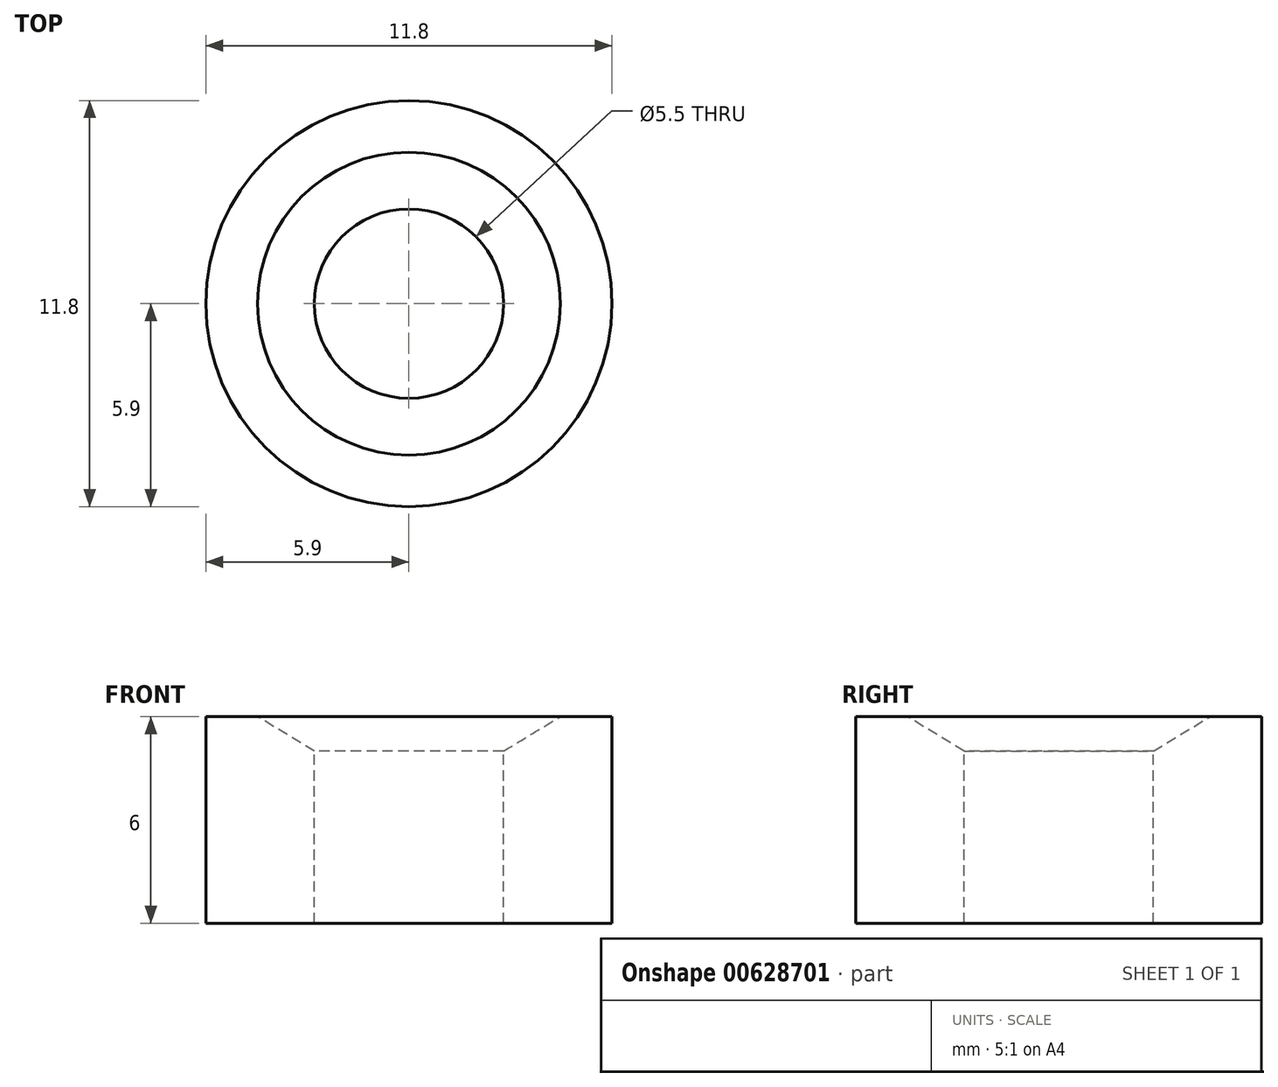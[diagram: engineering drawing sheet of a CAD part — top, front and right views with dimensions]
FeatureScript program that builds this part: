
annotation { "Feature Type Name" : "Feature", "Feature Type Description" : "" }
export const myFeature = defineFeature(function(context is Context, id is Id, definition is map)
    precondition{}
    {
        {
            var Q0;
            Q0=qCreatedBy(makeId("Front.planeOp"),FACE);
            var sketch = newSketch(context, id + "F0", { "sketchPlane" : qUnion([Q0])});
            skLineSegment(sketch, "E0", {"start": v(0, 40.85) * mm, "end": v(0, -41.9) * mm, "construction": true});
            skLineSegment(sketch, "E1", {"start": v(-5.9, 3) * mm, "end": v(-4.4, 3) * mm});
            skLineSegment(sketch, "E2", {"start": v(-4.4, 3) * mm, "end": v(-2.75, 2) * mm});
            skLineSegment(sketch, "E3", {"start": v(-2.75, 2) * mm, "end": v(-2.75, -3) * mm});
            skLineSegment(sketch, "E4", {"start": v(-2.75, -3) * mm, "end": v(-5.9, -3) * mm});
            skLineSegment(sketch, "E5", {"start": v(-5.9, -3) * mm, "end": v(-5.9, 3) * mm});
            skSolve(sketch);
        }
        {
            var Q0;
            Q0 = qSketchRegion(id + "F0", true);
            var Q1;
            Q1=sQuery(id+"F0.wireOp",EDGE,"E0");
            revolve(context, id + "F1", {"entities" : qUnion([Q0]), "axis" : qUnion([Q1]), "revolveType" : RevolveType.FULL});
        }
    });
